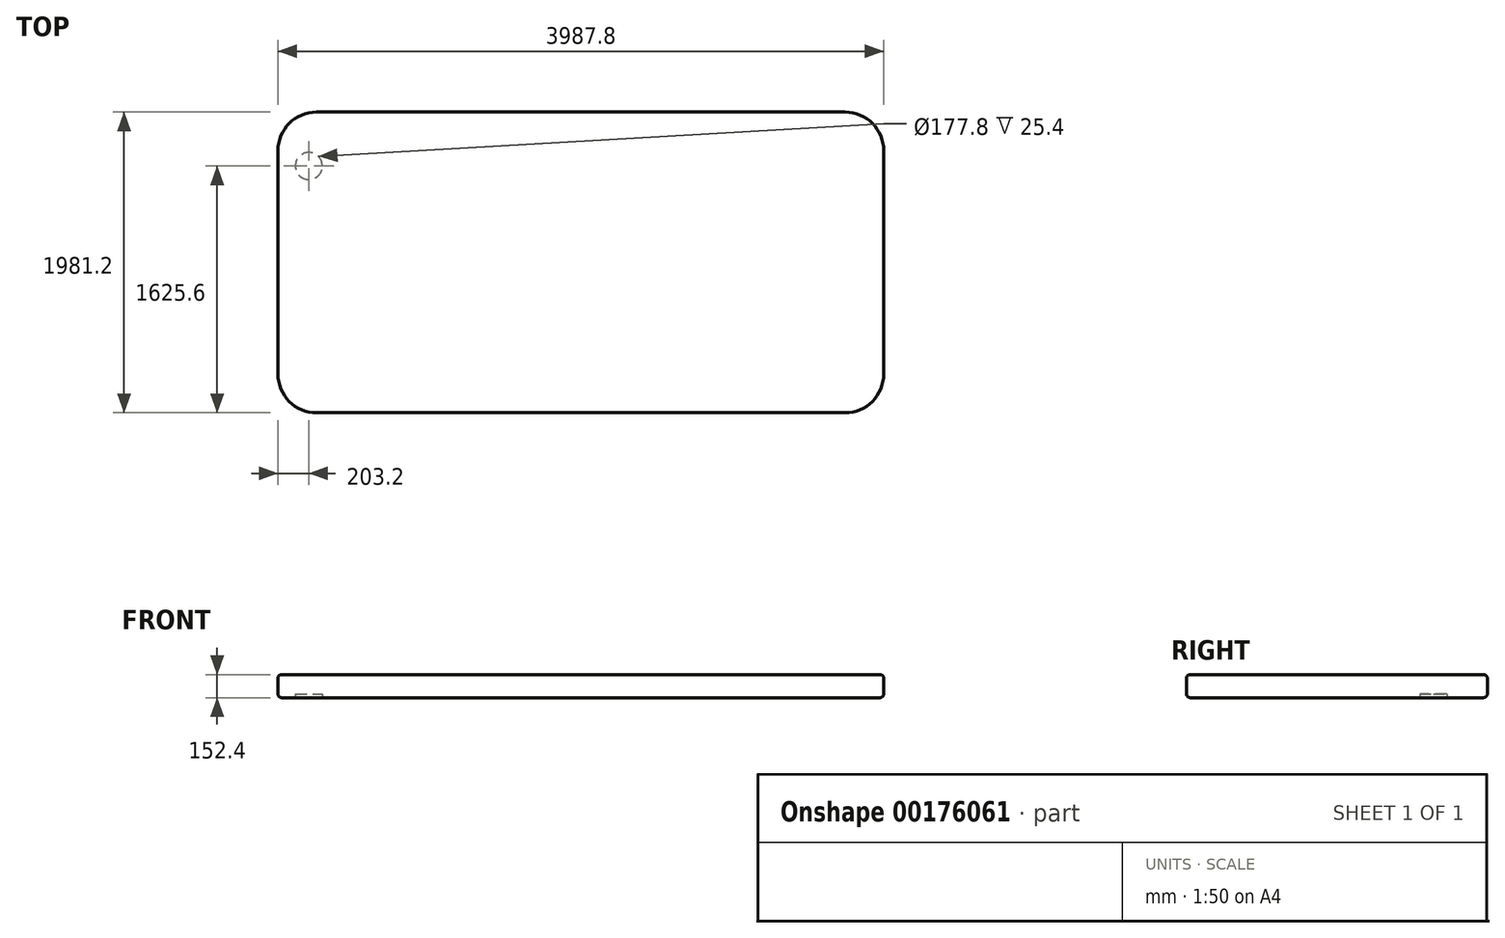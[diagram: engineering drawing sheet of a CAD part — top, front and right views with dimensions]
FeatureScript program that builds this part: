
annotation { "Feature Type Name" : "Feature", "Feature Type Description" : "" }
export const myFeature = defineFeature(function(context is Context, id is Id, definition is map)
    precondition{}
    {
        {
            var Q0;
            Q0=qCreatedBy(makeId("Front.planeOp"),FACE);
            var sketch = newSketch(context, id + "F0", { "sketchPlane" : qUnion([Q0])});
            skLineSegment(sketch, "E0.bottom", {"start": v(1993.9, -76.2) * mm, "end": v(-1993.9, -76.2) * mm});
            skLineSegment(sketch, "E0.top", {"start": v(1993.9, 76.2) * mm, "end": v(-1993.9, 76.2) * mm});
            skLineSegment(sketch, "E0.left", {"start": v(1993.9, -76.2) * mm, "end": v(1993.9, 76.2) * mm});
            skLineSegment(sketch, "E0.right", {"start": v(-1993.9, -76.2) * mm, "end": v(-1993.9, 76.2) * mm});
            skPoint(sketch, "E0.middle", {"position": v(0, 0) * mm});
            skSolve(sketch);
        }
        {
            var Q0;
            Q0=makeQuery(id+"F0.imprint","IMPRINT",FACE,{"disambiguationData":[TD([[makeQuery(id+"F0.imprint","IMPRINT",EDGE,{"derivedFrom":sQuery(id+"F0.wireOp",EDGE,"E0.bottom")}),-1.0]])]});
            extrude(context, id + "F1", {"entities" : qUnion([Q0]), "endBound" : BoundingType.SYMMETRIC, "oppositeDirection" : true, "depth" : 1981.2 * mm});
        }
        {
            var Q0;
            Q0=makeQuery(id+"F1.opExtrude","CAP_EDGE",EDGE,{"disambiguationData":[OSD([sQuery(id+"F0.wireOp",EDGE,"E0.right")])],"isStart":true});
            var Q1;
            Q1=makeQuery(id+"F1.opExtrude","CAP_EDGE",EDGE,{"disambiguationData":[OSD([sQuery(id+"F0.wireOp",EDGE,"E0.left")])],"isStart":true});
            var Q2;
            Q2=makeQuery(id+"F1.opExtrude","CAP_EDGE",EDGE,{"disambiguationData":[OSD([sQuery(id+"F0.wireOp",EDGE,"E0.left")])],"isStart":false});
            fillet(context, id + "F2", {"entities" : qUnion([Q0, Q1, Q2]), "radius" : 254 * mm, "tangentPropagation" : true, "allowEdgeOverflow" : false});
        }
        {
            var Q0;
            Q0=makeQuery(id+"F1.opExtrude","CAP_EDGE",EDGE,{"disambiguationData":[OSD([sQuery(id+"F0.wireOp",EDGE,"E0.right")])],"isStart":false});
            fillet(context, id + "F3", {"entities" : qUnion([Q0]), "radius" : 254 * mm, "tangentPropagation" : true, "allowEdgeOverflow" : false});
        }
        {
            var Q0;
            Q0=makeQuery(id+"F1.opExtrude","CAP_EDGE",EDGE,{"disambiguationData":[OSD([sQuery(id+"F0.wireOp",EDGE,"E0.bottom")])],"isStart":true});
            var Q1;
            Q1=makeQuery(id+"F2.opFillet","BLEND_EDGE",EDGE,{"blendedFrom":[makeQuery(id+"F1.opExtrude","CAP_EDGE",EDGE,{"disambiguationData":[OSD([sQuery(id+"F0.wireOp",EDGE,"E0.left")])],"isStart":true}),makeQuery(id+"F1.opExtrude","SWEPT_FACE",FACE,{"disambiguationData":[OSD([sQuery(id+"F0.wireOp",EDGE,"E0.bottom")])]})],"blendedInto":[makeQuery(id+"F1.opExtrude","SWEPT_FACE",FACE,{"disambiguationData":[OSD([sQuery(id+"F0.wireOp",EDGE,"E0.bottom")])]})]});
            var Q2;
            Q2=makeQuery(id+"F1.opExtrude","SWEPT_EDGE",EDGE,{"disambiguationData":[OSD([sQuery(id+"F0.wireOp",EDGE,"E0.bottom"),sQuery(id+"F0.wireOp",EDGE,"E0.left")])]});
            var Q3;
            Q3=makeQuery(id+"F2.opFillet","BLEND_EDGE",EDGE,{"blendedFrom":[makeQuery(id+"F1.opExtrude","CAP_EDGE",EDGE,{"disambiguationData":[OSD([sQuery(id+"F0.wireOp",EDGE,"E0.left")])],"isStart":false}),makeQuery(id+"F1.opExtrude","SWEPT_FACE",FACE,{"disambiguationData":[OSD([sQuery(id+"F0.wireOp",EDGE,"E0.bottom")])]})],"blendedInto":[makeQuery(id+"F1.opExtrude","SWEPT_FACE",FACE,{"disambiguationData":[OSD([sQuery(id+"F0.wireOp",EDGE,"E0.bottom")])]})]});
            var Q4;
            Q4=makeQuery(id+"F1.opExtrude","CAP_EDGE",EDGE,{"disambiguationData":[OSD([sQuery(id+"F0.wireOp",EDGE,"E0.bottom")])],"isStart":false});
            var Q5;
            Q5=makeQuery(id+"F3.opFillet","BLEND_EDGE",EDGE,{"blendedFrom":[makeQuery(id+"F1.opExtrude","CAP_EDGE",EDGE,{"disambiguationData":[OSD([sQuery(id+"F0.wireOp",EDGE,"E0.right")])],"isStart":false}),makeQuery(id+"F1.opExtrude","SWEPT_FACE",FACE,{"disambiguationData":[OSD([sQuery(id+"F0.wireOp",EDGE,"E0.bottom")])]})],"blendedInto":[makeQuery(id+"F1.opExtrude","SWEPT_FACE",FACE,{"disambiguationData":[OSD([sQuery(id+"F0.wireOp",EDGE,"E0.bottom")])]})]});
            var Q6;
            Q6=makeQuery(id+"F1.opExtrude","SWEPT_EDGE",EDGE,{"disambiguationData":[OSD([sQuery(id+"F0.wireOp",EDGE,"E0.bottom"),sQuery(id+"F0.wireOp",EDGE,"E0.right")])]});
            var Q7;
            Q7=makeQuery(id+"F2.opFillet","BLEND_EDGE",EDGE,{"blendedFrom":[makeQuery(id+"F1.opExtrude","CAP_EDGE",EDGE,{"disambiguationData":[OSD([sQuery(id+"F0.wireOp",EDGE,"E0.right")])],"isStart":true}),makeQuery(id+"F1.opExtrude","SWEPT_FACE",FACE,{"disambiguationData":[OSD([sQuery(id+"F0.wireOp",EDGE,"E0.bottom")])]})],"blendedInto":[makeQuery(id+"F1.opExtrude","SWEPT_FACE",FACE,{"disambiguationData":[OSD([sQuery(id+"F0.wireOp",EDGE,"E0.bottom")])]})]});
            fillet(context, id + "F4", {"entities" : qUnion([Q0, Q1, Q2, Q3, Q4, Q5, Q6, Q7]), "radius" : 25.4 * mm, "tangentPropagation" : true, "allowEdgeOverflow" : false});
        }
        {
            var Q0;
            Q0=makeQuery(id+"F2.opFillet","BLEND_EDGE",EDGE,{"blendedFrom":[makeQuery(id+"F1.opExtrude","CAP_EDGE",EDGE,{"disambiguationData":[OSD([sQuery(id+"F0.wireOp",EDGE,"E0.left")])],"isStart":true}),makeQuery(id+"F1.opExtrude","SWEPT_FACE",FACE,{"disambiguationData":[OSD([sQuery(id+"F0.wireOp",EDGE,"E0.top")])]})],"blendedInto":[makeQuery(id+"F1.opExtrude","SWEPT_FACE",FACE,{"disambiguationData":[OSD([sQuery(id+"F0.wireOp",EDGE,"E0.top")])]})]});
            var Q1;
            Q1=makeQuery(id+"F1.opExtrude","CAP_EDGE",EDGE,{"disambiguationData":[OSD([sQuery(id+"F0.wireOp",EDGE,"E0.top")])],"isStart":true});
            var Q2;
            Q2=makeQuery(id+"F2.opFillet","BLEND_EDGE",EDGE,{"blendedFrom":[makeQuery(id+"F1.opExtrude","CAP_EDGE",EDGE,{"disambiguationData":[OSD([sQuery(id+"F0.wireOp",EDGE,"E0.right")])],"isStart":true}),makeQuery(id+"F1.opExtrude","SWEPT_FACE",FACE,{"disambiguationData":[OSD([sQuery(id+"F0.wireOp",EDGE,"E0.top")])]})],"blendedInto":[makeQuery(id+"F1.opExtrude","SWEPT_FACE",FACE,{"disambiguationData":[OSD([sQuery(id+"F0.wireOp",EDGE,"E0.top")])]})]});
            var Q3;
            Q3=makeQuery(id+"F1.opExtrude","SWEPT_EDGE",EDGE,{"disambiguationData":[OSD([sQuery(id+"F0.wireOp",EDGE,"E0.top"),sQuery(id+"F0.wireOp",EDGE,"E0.right")])]});
            var Q4;
            Q4=makeQuery(id+"F3.opFillet","BLEND_EDGE",EDGE,{"blendedFrom":[makeQuery(id+"F1.opExtrude","CAP_EDGE",EDGE,{"disambiguationData":[OSD([sQuery(id+"F0.wireOp",EDGE,"E0.right")])],"isStart":false}),makeQuery(id+"F1.opExtrude","SWEPT_FACE",FACE,{"disambiguationData":[OSD([sQuery(id+"F0.wireOp",EDGE,"E0.top")])]})],"blendedInto":[makeQuery(id+"F1.opExtrude","SWEPT_FACE",FACE,{"disambiguationData":[OSD([sQuery(id+"F0.wireOp",EDGE,"E0.top")])]})]});
            var Q5;
            Q5=makeQuery(id+"F1.opExtrude","CAP_EDGE",EDGE,{"disambiguationData":[OSD([sQuery(id+"F0.wireOp",EDGE,"E0.top")])],"isStart":false});
            var Q6;
            Q6=makeQuery(id+"F2.opFillet","BLEND_EDGE",EDGE,{"blendedFrom":[makeQuery(id+"F1.opExtrude","CAP_EDGE",EDGE,{"disambiguationData":[OSD([sQuery(id+"F0.wireOp",EDGE,"E0.left")])],"isStart":false}),makeQuery(id+"F1.opExtrude","SWEPT_FACE",FACE,{"disambiguationData":[OSD([sQuery(id+"F0.wireOp",EDGE,"E0.top")])]})],"blendedInto":[makeQuery(id+"F1.opExtrude","SWEPT_FACE",FACE,{"disambiguationData":[OSD([sQuery(id+"F0.wireOp",EDGE,"E0.top")])]})]});
            var Q7;
            Q7=makeQuery(id+"F1.opExtrude","SWEPT_EDGE",EDGE,{"disambiguationData":[OSD([sQuery(id+"F0.wireOp",EDGE,"E0.top"),sQuery(id+"F0.wireOp",EDGE,"E0.left")])]});
            fillet(context, id + "F5", {"entities" : qUnion([Q0, Q1, Q2, Q3, Q4, Q5, Q6, Q7]), "radius" : 25.4 * mm, "tangentPropagation" : true, "allowEdgeOverflow" : false});
        }
        {
            var Q0;
            Q0=makeQuery(id+"F1.opExtrude","SWEPT_FACE",FACE,{"disambiguationData":[OSD([sQuery(id+"F0.wireOp",EDGE,"E0.bottom")])]});
            var sketch = newSketch(context, id + "F6", { "sketchPlane" : qUnion([Q0])});
            skLineSegment(sketch, "E1", {"start": v(-1968.5, -635) * mm, "end": v(-1790.7, -635) * mm, "construction": true});
            skLineSegment(sketch, "E2", {"start": v(-1790.7, -635) * mm, "end": v(-1790.7, -965.2) * mm, "construction": true});
            skCircle(sketch, "E3", {"center": v(-1790.7, -635) * mm, "radius": 88.9 * mm});
            skSolve(sketch);
        }
        {
            var Q0;
            Q0=makeQuery(id+"F6.imprint","IMPRINT",FACE,{"disambiguationData":[TD([[makeQuery(id+"F6.imprint","IMPRINT",EDGE,{"derivedFrom":sQuery(id+"F6.wireOp",EDGE,"E3")}),1.0]])]});
            var Q1;
            Q1=sQuery(id+"F6.wireOp",EDGE,"E3");
            extrude(context, id + "F7", {"entities" : qUnion([Q0]), "operationType" : NewBodyOperationType.REMOVE, "surfaceEntities" : qUnion([Q1]), "oppositeDirection" : true, "depth" : 25.4 * mm});
        }
    });
